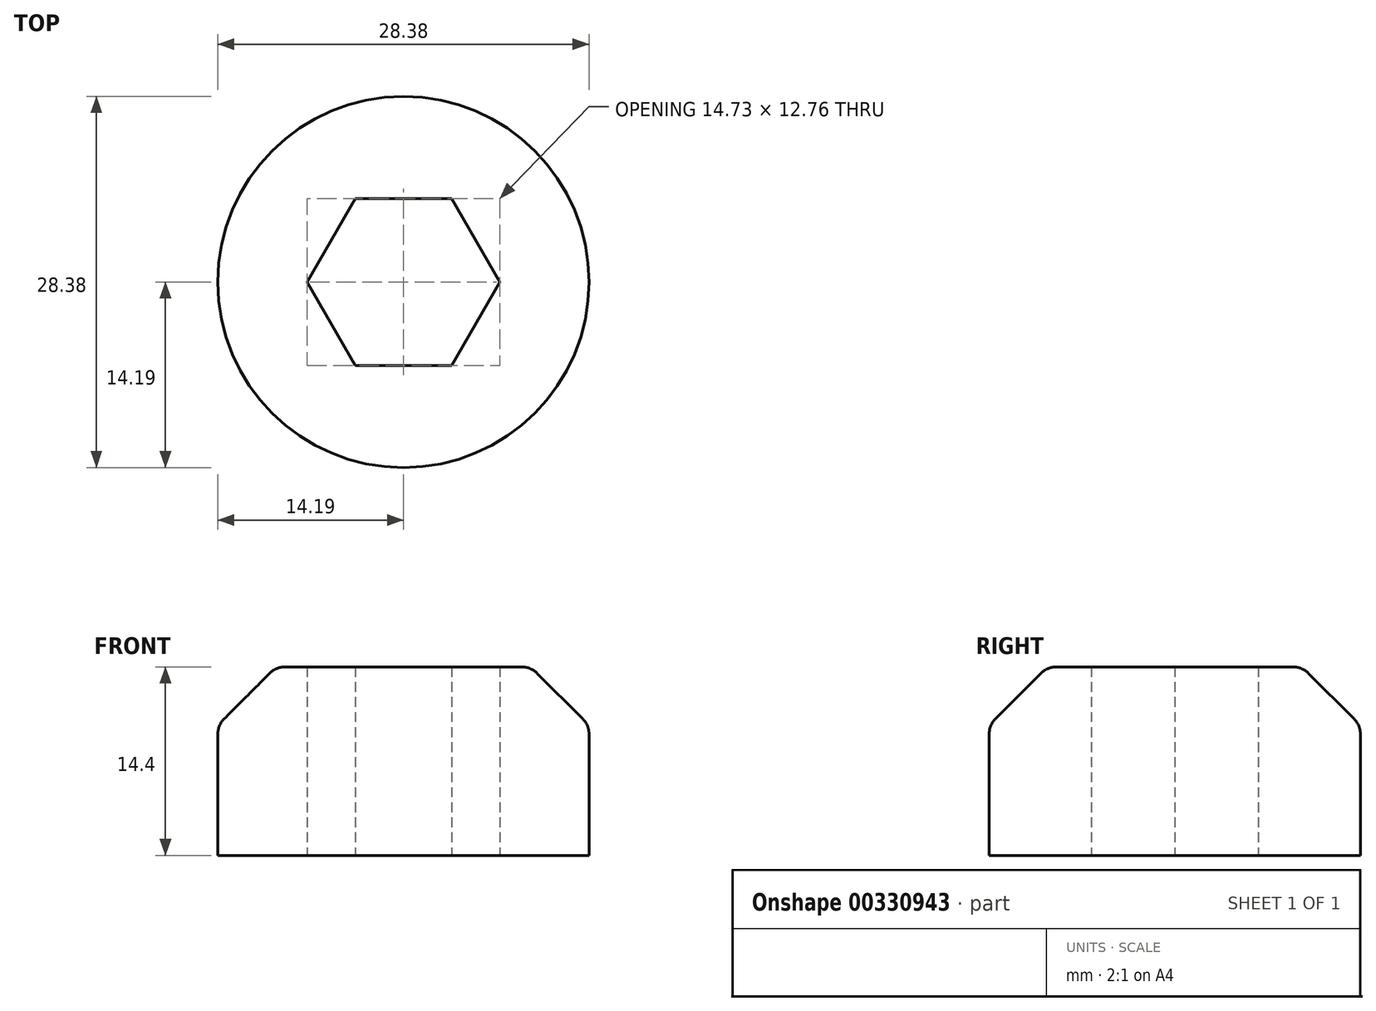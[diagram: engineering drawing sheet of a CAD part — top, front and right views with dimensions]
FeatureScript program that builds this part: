
annotation { "Feature Type Name" : "Feature", "Feature Type Description" : "" }
export const myFeature = defineFeature(function(context is Context, id is Id, definition is map)
    precondition{}
    {
        {
            var Q0;
            Q0=qCreatedBy(makeId("Top.planeOp"),FACE);
            var sketch = newSketch(context, id + "F0", { "sketchPlane" : qUnion([Q0])});
            skCircle(sketch, "E0", {"center": v(0, 0) * mm, "radius": 14.19 * mm});
            skCircle(sketch, "E1.cCircle", {"center": v(0, 0) * mm, "radius": 6.38 * mm, "construction": true});
            skLineSegment(sketch, "E1.0", {"start": v(-3.68, 6.38) * mm, "end": v(3.68, 6.38) * mm});
            skLineSegment(sketch, "E1.1", {"start": v(3.68, 6.38) * mm, "end": v(7.37, 0) * mm});
            skLineSegment(sketch, "E1.2", {"start": v(7.37, 0) * mm, "end": v(3.68, -6.38) * mm});
            skLineSegment(sketch, "E1.3", {"start": v(3.68, -6.38) * mm, "end": v(-3.68, -6.38) * mm});
            skLineSegment(sketch, "E1.4", {"start": v(-3.68, -6.38) * mm, "end": v(-7.37, 0) * mm});
            skLineSegment(sketch, "E1.5", {"start": v(-7.37, 0) * mm, "end": v(-3.68, 6.38) * mm});
            skPoint(sketch, "E1.0.midPoint", {"position": v(0, 6.38) * mm});
            skSolve(sketch);
        }
        {
            var Q0;
            Q0=qSketchRegion(id+"F0",true);
            var Q1;
            Q1=makeQuery(id+"F0.imprint","IMPRINT",FACE,{"disambiguationData":[TD([[makeQuery(id+"F0.imprint","IMPRINT",EDGE,{"derivedFrom":sQuery(id+"F0.wireOp",EDGE,"31cd7da6-dbf0-4eda-b4b2-b3da4ef2fe02.0")}),1.0]])]});
            extrude(context, id + "F1", {"entities" : qUnion([Q0, Q1]), "depth" : 14.4 * mm});
        }
        {
            var Q0;
            Q0=makeQuery(id+"F1.opExtrude","CAP_EDGE",EDGE,{"disambiguationData":[OSD([sQuery(id+"F0.wireOp",EDGE,"E0")])],"isStart":false});
            chamfer(context, id + "F2", {"entities" : qUnion([Q0]), "width" : 4.44 * mm, "tangentPropagation" : true});
        }
        {
            var Q0;
            {var subQ0=sQuery(id+"F0.wireOp",EDGE,"E0");Q0=makeQuery(id+"F2.opChamfer","BLEND_EDGE",EDGE,{"blendedFrom":[makeQuery(id+"F1.opExtrude","CAP_EDGE",EDGE,{"disambiguationData":[OSD([subQ0])],"isStart":false}),makeQuery(id+"F1.opExtrude","CAP_FACE",FACE,{"disambiguationData":[OSD([subQ0,sQuery(id+"F0.wireOp",EDGE,"E1.0"),sQuery(id+"F0.wireOp",EDGE,"E1.1"),sQuery(id+"F0.wireOp",EDGE,"E1.2"),sQuery(id+"F0.wireOp",EDGE,"E1.3"),sQuery(id+"F0.wireOp",EDGE,"E1.4"),sQuery(id+"F0.wireOp",EDGE,"E1.5")])],"isStart":false})],"blendedInto":[makeQuery(id+"F1.opExtrude","CAP_FACE",FACE,{"disambiguationData":[OSD([subQ0,sQuery(id+"F0.wireOp",EDGE,"E1.0"),sQuery(id+"F0.wireOp",EDGE,"E1.1"),sQuery(id+"F0.wireOp",EDGE,"E1.2"),sQuery(id+"F0.wireOp",EDGE,"E1.3"),sQuery(id+"F0.wireOp",EDGE,"E1.4"),sQuery(id+"F0.wireOp",EDGE,"E1.5")])],"isStart":false})]});}
            var Q1;
            {var subQ0=sQuery(id+"F0.wireOp",EDGE,"E0");Q1=makeQuery(id+"F2.opChamfer","BLEND_EDGE",EDGE,{"blendedFrom":[makeQuery(id+"F1.opExtrude","CAP_EDGE",EDGE,{"disambiguationData":[OSD([subQ0])],"isStart":false}),makeQuery(id+"F1.opExtrude","SWEPT_FACE",FACE,{"disambiguationData":[OSD([subQ0])]})],"blendedInto":[makeQuery(id+"F1.opExtrude","SWEPT_FACE",FACE,{"disambiguationData":[OSD([subQ0])]})]});}
            fillet(context, id + "F3", {"entities" : qUnion([Q0, Q1]), "radius" : 1.59 * mm, "tangentPropagation" : true, "allowEdgeOverflow" : false});
        }
    });
